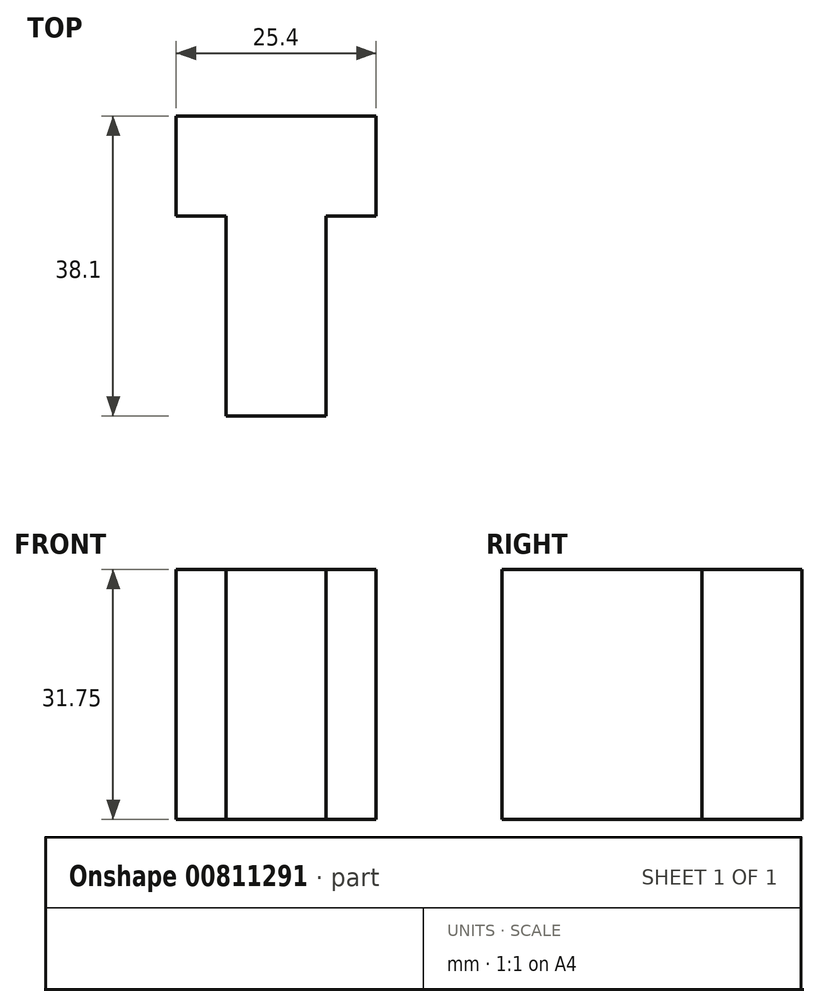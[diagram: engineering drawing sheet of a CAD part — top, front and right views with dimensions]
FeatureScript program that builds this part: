
annotation { "Feature Type Name" : "Feature", "Feature Type Description" : "" }
export const myFeature = defineFeature(function(context is Context, id is Id, definition is map)
    precondition{}
    {
        {
            var Q0;
            Q0=qCreatedBy(makeId("Top.planeOp"),FACE);
            var sketch = newSketch(context, id + "F0", { "sketchPlane" : qUnion([Q0])});
            skLineSegment(sketch, "E0", {"start": v(70.17, 72.12) * mm, "end": v(70.17, 61.5) * mm});
            skLineSegment(sketch, "E1", {"start": v(0, 0) * mm, "end": v(0, 25.4) * mm});
            skLineSegment(sketch, "E2", {"start": v(0, 25.4) * mm, "end": v(-6.35, 25.4) * mm});
            skLineSegment(sketch, "E3", {"start": v(-6.35, 25.4) * mm, "end": v(-6.35, 38.1) * mm});
            skLineSegment(sketch, "E4", {"start": v(-6.35, 38.1) * mm, "end": v(0, 38.1) * mm});
            skLineSegment(sketch, "E5", {"start": v(0, 38.1) * mm, "end": v(19.05, 38.1) * mm});
            skLineSegment(sketch, "E6", {"start": v(19.05, 38.1) * mm, "end": v(19.05, 25.4) * mm});
            skLineSegment(sketch, "E7", {"start": v(19.05, 25.4) * mm, "end": v(12.7, 25.4) * mm});
            skLineSegment(sketch, "E8", {"start": v(12.7, 25.4) * mm, "end": v(12.7, 0) * mm});
            skLineSegment(sketch, "E9", {"start": v(12.7, 0) * mm, "end": v(0, 0) * mm});
            skSolve(sketch);
        }
        {
            var Q0;
            Q0=makeQuery(id+"F0.imprint","IMPRINT",FACE,{"disambiguationData":[TD([[makeQuery(id+"F0.imprint","IMPRINT",EDGE,{"derivedFrom":sQuery(id+"F0.wireOp",EDGE,"E1")}),-1.0]])]});
            extrude(context, id + "F1", {"entities" : qUnion([Q0]), "oppositeDirection" : true, "depth" : 31.75 * mm, "offsetDistance" : 25.4 * mm});
        }
    });
